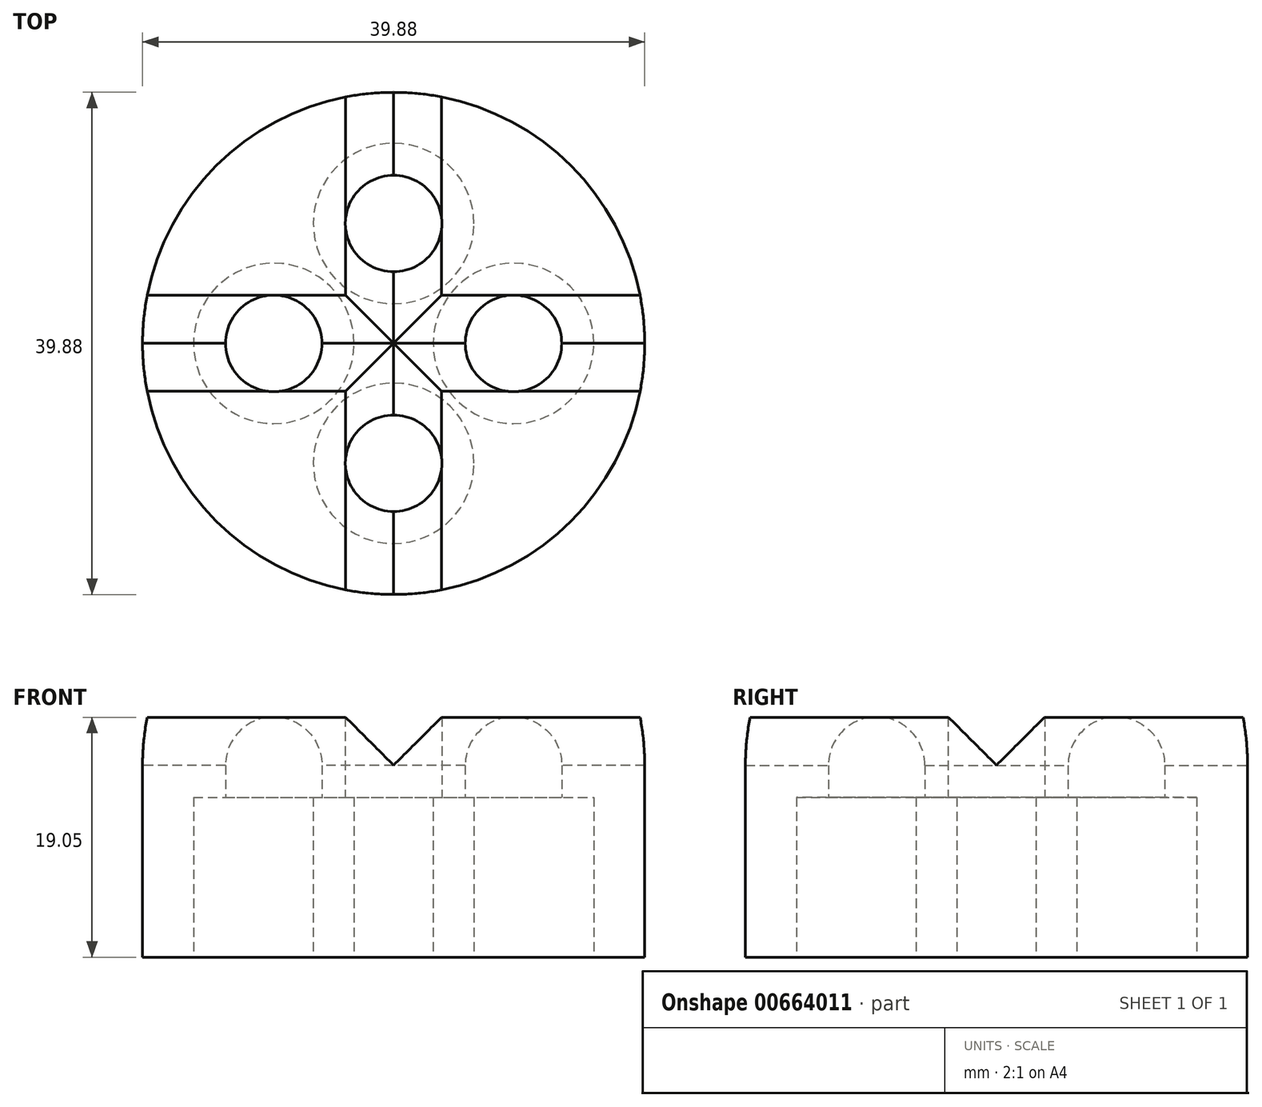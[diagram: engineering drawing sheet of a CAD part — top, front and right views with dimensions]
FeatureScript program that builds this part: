
annotation { "Feature Type Name" : "Feature", "Feature Type Description" : "" }
export const myFeature = defineFeature(function(context is Context, id is Id, definition is map)
    precondition{}
    {
        {
            var Q0;
            Q0=qCreatedBy(makeId("Top.planeOp"),FACE);
            var sketch = newSketch(context, id + "F0", { "sketchPlane" : qUnion([Q0])});
            skCircle(sketch, "E0", {"center": v(0, 0) * mm, "radius": 19.94 * mm});
            skSolve(sketch);
        }
        {
            var Q0;
            Q0=makeQuery(id+"F0.imprint","IMPRINT",FACE,{"disambiguationData":[TD([[makeQuery(id+"F0.imprint","IMPRINT",EDGE,{"derivedFrom":sQuery(id+"F0.wireOp",EDGE,"E0")}),1.0]])]});
            extrude(context, id + "F1", {"entities" : qUnion([Q0]), "depth" : 19.05 * mm, "offsetDistance" : 25.4 * mm});
        }
        {
            var Q0;
            Q0=qCreatedBy(makeId("Front.planeOp"),FACE);
            var sketch = newSketch(context, id + "F2", { "sketchPlane" : qUnion([Q0])});
            skLineSegment(sketch, "E1", {"start": v(0, 68.6) * mm, "end": v(0, -61.21) * mm, "construction": true});
            skSolve(sketch);
        }
        {
            var Q0;
            Q0=makeQuery(id+"F1.opExtrude","CAP_FACE",FACE,{"disambiguationData":[OSD([sQuery(id+"F0.wireOp",EDGE,"E0")])],"isStart":true});
            var sketch = newSketch(context, id + "F3", { "sketchPlane" : qUnion([Q0])});
            skLineSegment(sketch, "E2", {"start": v(0, -9.52) * mm, "end": v(9.52, 0) * mm, "construction": true});
            skLineSegment(sketch, "E3", {"start": v(-9.52, 0) * mm, "end": v(0, 9.52) * mm, "construction": true});
            skLineSegment(sketch, "E4", {"start": v(-9.52, 0) * mm, "end": v(0, -9.52) * mm, "construction": true});
            skLineSegment(sketch, "E5", {"start": v(0, 9.52) * mm, "end": v(9.52, 0) * mm, "construction": true});
            skCircle(sketch, "E6", {"center": v(-9.52, 0) * mm, "radius": 6.38 * mm});
            skCircle(sketch, "E7", {"center": v(0, 9.52) * mm, "radius": 6.38 * mm});
            skCircle(sketch, "E8", {"center": v(9.52, 0) * mm, "radius": 6.38 * mm});
            skCircle(sketch, "E9", {"center": v(0, -9.52) * mm, "radius": 6.38 * mm});
            skSolve(sketch);
        }
        {
            var Q0;
            Q0 = qSketchRegion(id + "F3", true);
            extrude(context, id + "F4", {"entities" : qUnion([Q0]), "operationType" : NewBodyOperationType.REMOVE, "oppositeDirection" : true, "depth" : 12.7 * mm, "offsetDistance" : 25.4 * mm});
        }
        {
            var Q0;
            Q0=makeQuery(id+"F4.boolean.opBoolean","COPY",FACE,{"derivedFrom":makeQuery(id+"F4.opExtrude","CAP_FACE",FACE,{"disambiguationData":[OSD([sQuery(id+"F3.wireOp",EDGE,"E7")])],"isStart":false})});
            var sketch = newSketch(context, id + "F5", { "sketchPlane" : qUnion([Q0])});
            skCircle(sketch, "E10.0", {"center": v(0, 9.52) * mm, "radius": 3.84 * mm});
            skCircle(sketch, "E11.0", {"center": v(-9.52, 0) * mm, "radius": 3.84 * mm});
            skCircle(sketch, "E12.0", {"center": v(0, -9.52) * mm, "radius": 3.84 * mm});
            skCircle(sketch, "E13.0", {"center": v(9.52, 0) * mm, "radius": 3.84 * mm});
            skSolve(sketch);
        }
        {
            var Q0;
            Q0 = qSketchRegion(id + "F5", true);
            extrude(context, id + "F6", {"entities" : qUnion([Q0]), "operationType" : NewBodyOperationType.REMOVE, "endBound" : BoundingType.THROUGH_ALL, "oppositeDirection" : true, "depth" : 25.4 * mm, "offsetDistance" : 25.4 * mm});
        }
        {
            var Q0;
            Q0=qCreatedBy(makeId("Front.planeOp"),FACE);
            var sketch = newSketch(context, id + "F7", { "sketchPlane" : qUnion([Q0])});
            skPoint(sketch, "E14", {"position": v(0, 15.24) * mm});
            skLineSegment(sketch, "E15", {"start": v(0, 15.24) * mm, "end": v(-8.64, 23.88) * mm});
            skLineSegment(sketch, "E16", {"start": v(-8.64, 23.88) * mm, "end": v(8.64, 23.88) * mm});
            skLineSegment(sketch, "E17", {"start": v(8.64, 23.88) * mm, "end": v(0, 15.24) * mm});
            skSolve(sketch);
        }
        {
            var Q0;
            Q0 = qSketchRegion(id + "F7", true);
            extrude(context, id + "F8", {"entities" : qUnion([Q0]), "operationType" : NewBodyOperationType.REMOVE, "endBound" : BoundingType.SYMMETRIC, "depth" : 76.2 * mm, "offsetDistance" : 25.4 * mm});
        }
        {
            var Q0;
            Q0=qCreatedBy(makeId("Right.planeOp"),FACE);
            var sketch = newSketch(context, id + "F9", { "sketchPlane" : qUnion([Q0])});
            skPoint(sketch, "E18", {"position": v(0, 15.24) * mm});
            skLineSegment(sketch, "E19", {"start": v(0, 15.24) * mm, "end": v(-11.61, 26.85) * mm});
            skLineSegment(sketch, "E20", {"start": v(-11.61, 26.85) * mm, "end": v(11.61, 26.85) * mm});
            skLineSegment(sketch, "E21", {"start": v(11.61, 26.85) * mm, "end": v(0, 15.24) * mm});
            skSolve(sketch);
        }
        {
            var Q0;
            Q0 = qSketchRegion(id + "F9", true);
            extrude(context, id + "F10", {"entities" : qUnion([Q0]), "operationType" : NewBodyOperationType.REMOVE, "endBound" : BoundingType.SYMMETRIC, "depth" : 76.2 * mm, "offsetDistance" : 25.4 * mm});
        }
    });
